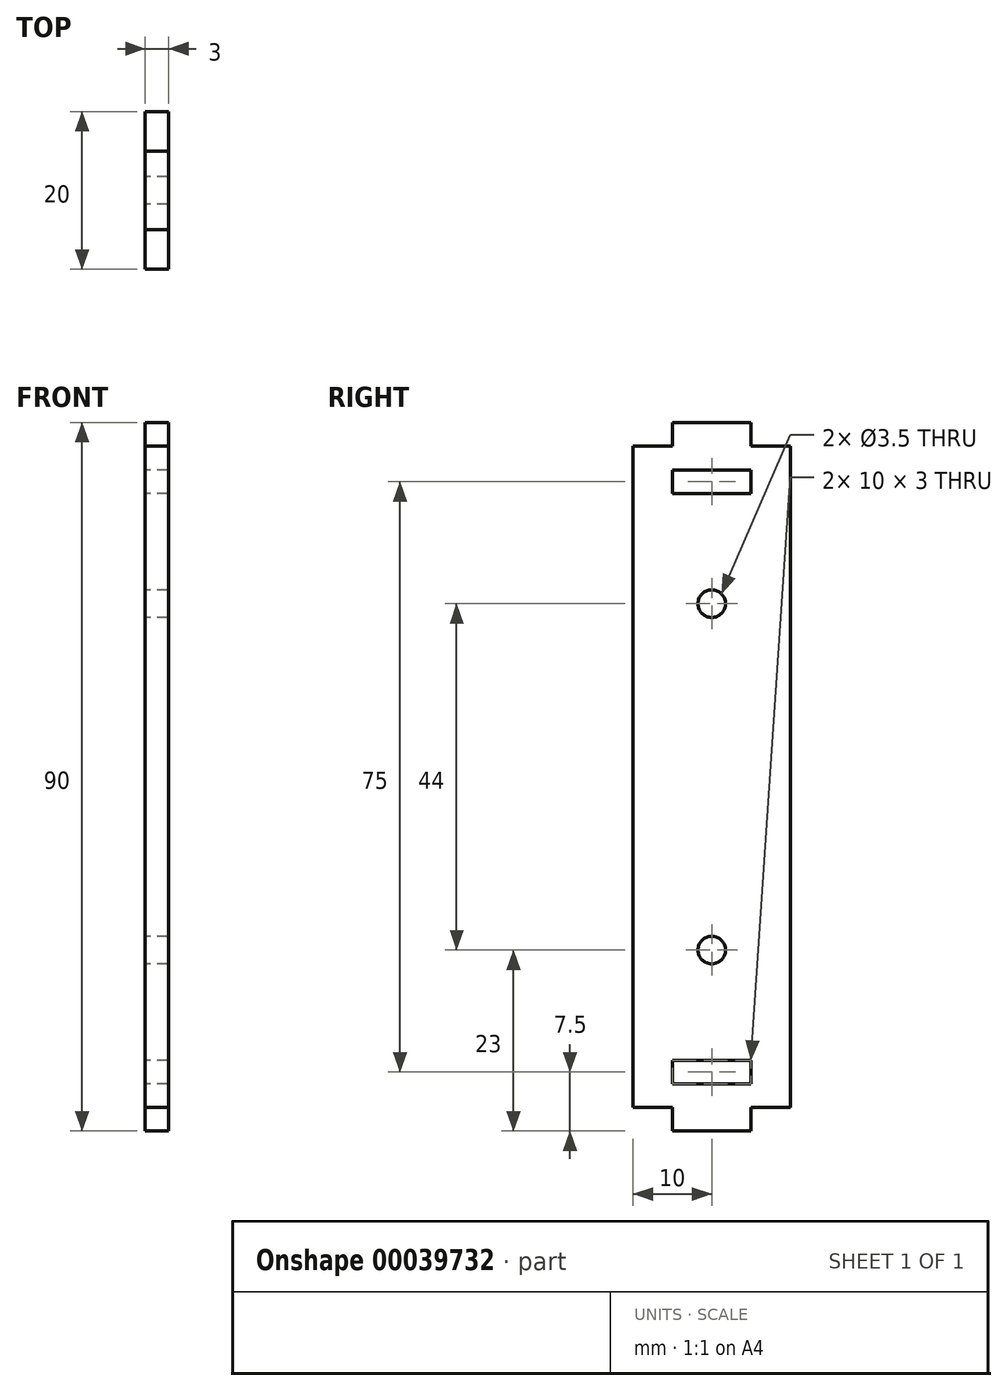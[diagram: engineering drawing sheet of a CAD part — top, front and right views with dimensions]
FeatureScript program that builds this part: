
annotation { "Feature Type Name" : "Feature", "Feature Type Description" : "" }
export const myFeature = defineFeature(function(context is Context, id is Id, definition is map)
    precondition{}
    {
        {
            var Q0;
            Q0=qCreatedBy(makeId("Right.planeOp"),FACE);
            var sketch = newSketch(context, id + "F0", { "sketchPlane" : qUnion([Q0])});
            skLineSegment(sketch, "E0.rect.bottom", {"start": v(10, 42) * mm, "end": v(-10, 42) * mm});
            skLineSegment(sketch, "E0.rect.top", {"start": v(10, -42) * mm, "end": v(-10, -42) * mm});
            skLineSegment(sketch, "E0.rect.left", {"start": v(10, 42) * mm, "end": v(10, -42) * mm});
            skLineSegment(sketch, "E0.rect.right", {"start": v(-10, 42) * mm, "end": v(-10, -42) * mm});
            skPoint(sketch, "E0.rect.middle", {"position": v(0, 0) * mm});
            skLineSegment(sketch, "E1.bottom", {"start": v(-5, 42) * mm, "end": v(5, 42) * mm});
            skLineSegment(sketch, "E1.top", {"start": v(-5, 45) * mm, "end": v(5, 45) * mm});
            skLineSegment(sketch, "E1.left", {"start": v(-5, 42) * mm, "end": v(-5, 45) * mm});
            skLineSegment(sketch, "E1.right", {"start": v(5, 42) * mm, "end": v(5, 45) * mm});
            skLineSegment(sketch, "E2.bottom", {"start": v(-5, -42) * mm, "end": v(5, -42) * mm});
            skLineSegment(sketch, "E2.top", {"start": v(-5, -45) * mm, "end": v(5, -45) * mm});
            skLineSegment(sketch, "E2.left", {"start": v(-5, -42) * mm, "end": v(-5, -45) * mm});
            skLineSegment(sketch, "E2.right", {"start": v(5, -42) * mm, "end": v(5, -45) * mm});
            skLineSegment(sketch, "E3.bottom", {"start": v(-5, -36) * mm, "end": v(5, -36) * mm});
            skLineSegment(sketch, "E3.top", {"start": v(-5, -39) * mm, "end": v(5, -39) * mm});
            skLineSegment(sketch, "E3.left", {"start": v(-5, -36) * mm, "end": v(-5, -39) * mm});
            skLineSegment(sketch, "E3.right", {"start": v(5, -36) * mm, "end": v(5, -39) * mm});
            skLineSegment(sketch, "E4.bottom", {"start": v(-5, 39) * mm, "end": v(5, 39) * mm});
            skLineSegment(sketch, "E4.top", {"start": v(-5, 36) * mm, "end": v(5, 36) * mm});
            skLineSegment(sketch, "E4.left", {"start": v(-5, 39) * mm, "end": v(-5, 36) * mm});
            skLineSegment(sketch, "E4.right", {"start": v(5, 39) * mm, "end": v(5, 36) * mm});
            skCircle(sketch, "E5", {"center": v(0, 22) * mm, "radius": 1.75 * mm});
            skPoint(sketch, "E5.centerSnap0", {"position": v(0, 36) * mm});
            skCircle(sketch, "E6", {"center": v(0, -22) * mm, "radius": 1.75 * mm});
            skPoint(sketch, "E6.centerSnap0", {"position": v(0, -36) * mm});
            skSolve(sketch);
        }
        {
            var Q0;
            Q0 = qSketchRegion(id + "F0", true);
            extrude(context, id + "F1", {"entities" : qUnion([Q0]), "depth" : 3 * mm});
        }
    });
